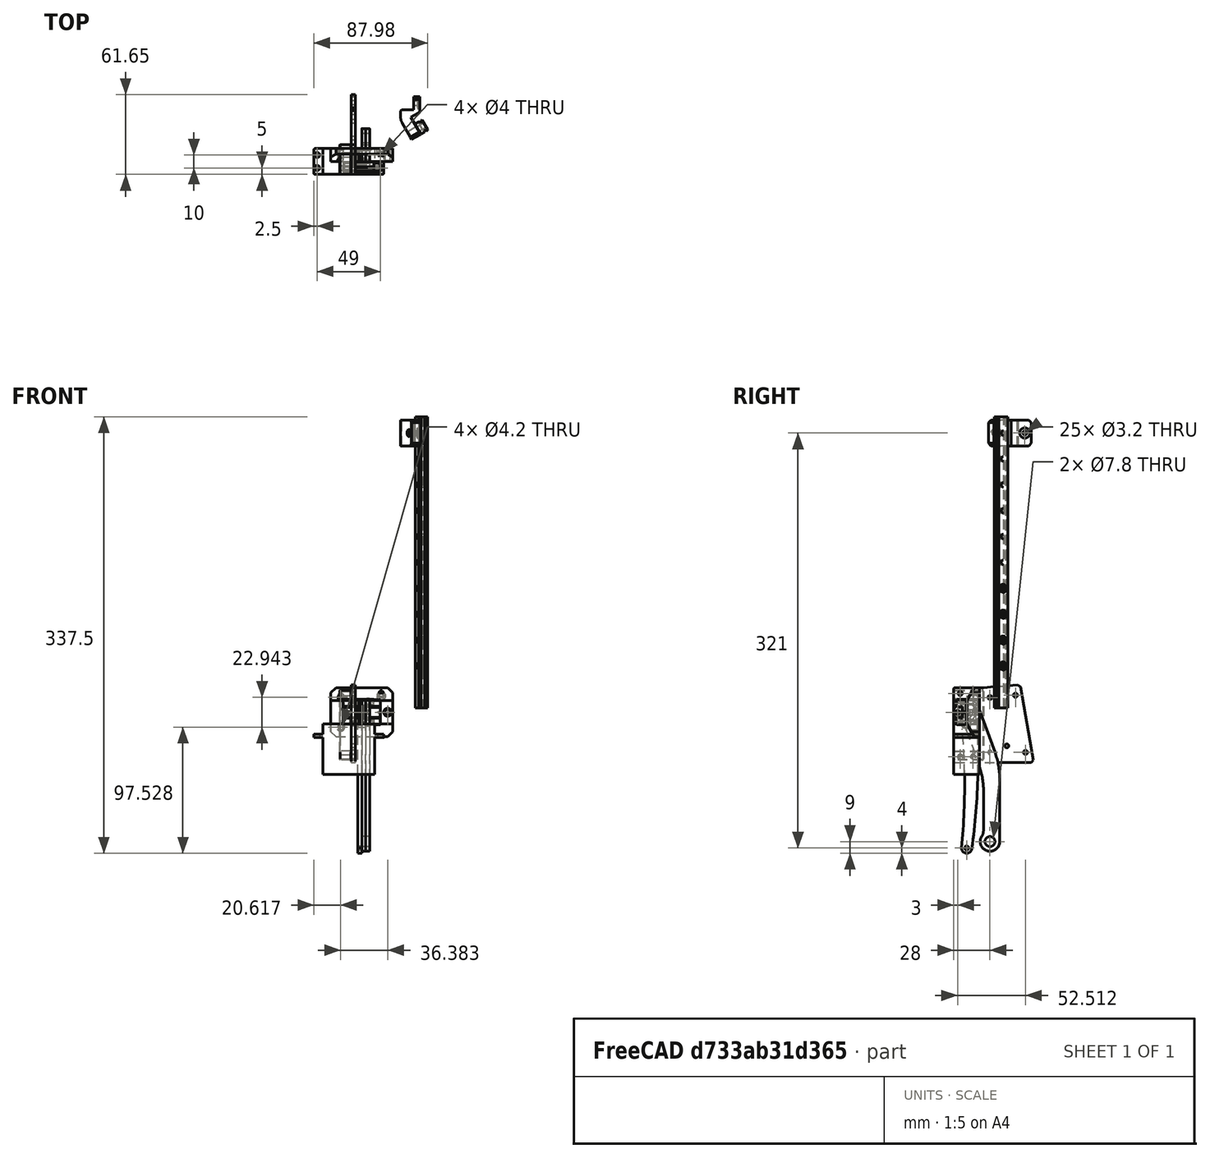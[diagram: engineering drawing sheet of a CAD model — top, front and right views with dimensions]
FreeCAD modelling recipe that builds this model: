
FCSTD DOCUMENT  (FreeCAD 1.2R20260106 (Git shallow))
Label: linear-lifter
License: All rights reserved
LicenseURL: https://en.wikipedia.org/wiki/All_rights_reserved
objects: App::FeaturePython×18, Part::Feature×15, App::Link×15, App::Point×5, App::Part×4, Assembly::JointGroup×1, Assembly::AssemblyObject×1
note: 15 computed .brp shape members not serialized (recipe doc carries the construction recipe); baked Part::Feature solids carry a one-line shape summary decoded from their .brp

FEATURE [Part::Feature] Part__Feature  label="ServoLifterPlate"
  Placement = pos=(-8,0,0) rot=(0,0,1;0rad)
  shape: bbox 3 x 61.65 x 60.3 mm, 21 faces (baked)
FEATURE [Part::Feature] Part__Feature001  label="ServoLifterSpacer"
  Placement = pos=(-8,0,0) rot=(0,0,1;0rad)
  shape: bbox 9 x 23 x 54 mm, 56 faces (baked)
FEATURE [Part::Feature] Part__Feature006  label="RoundServoHorn"
  Placement = pos=(2.274e-13,-5.72205e-06,3.05176e-05) rot=(0.171088,0.970288,0.171088;1.60095rad)
  shape: bbox 5.4 x 20 x 20 mm, 12 faces (baked)
FEATURE [Part::Feature] Part__Feature007  label="CoreMF83"
  shape: bbox 9.2 x 3 x 9.2 mm, 6 faces (baked)
FEATURE [Part::Feature] Part__Feature008  label="CoreMF001"
  shape: bbox 4.2 x 3 x 4.2 mm, 4 faces (baked)
FEATURE [App::Part] CoreMF83  label="CoreMF002"
  Group = -> [Part__Feature007,Part__Feature008]
  Origin = -> Origin002
FEATURE [App::Point] Origin003  label="Origine002"
  Role = Origin
FEATURE [Part::Feature] Part__Feature009  label="SleeveMF83"
  shape: bbox 6.8 x 2.8 x 6.8 mm, 4 faces (baked)
FEATURE [App::Part] MF83
  Group = -> [CoreMF83,Part__Feature009]
  Origin = -> Origin004
  Placement = pos=(-2.2769e-05,18,-100) rot=(0,0,1;1.5708rad)
FEATURE [App::Point] Origin005  label="Origine004"
  Role = Origin
FEATURE [Part::Feature] Part__Feature010  label="Bielle"
  Placement = pos=(3,-3.8147e-06,0) rot=(0,0,1;0rad)
  shape: bbox 3 x 35.5 x 117.5 mm, 18 faces (baked)
FEATURE [Part::Feature] Part__Feature011  label="Bielle001"
  shape: bbox 3 x 35.5 x 117.5 mm, 18 faces (baked)
FEATURE [Part::Feature] Part__Feature017  label="Body028"
  shape: bbox 3.367 x 16.32 x 116.5 mm, 9 faces (baked)
FEATURE [Part::Feature] Part__Feature018  label="ServoBody001"
  Placement = pos=(0,0,-1) rot=(0,0,1;0rad)
  shape: bbox 54 x 20 x 41 mm, 25 faces (baked)
FEATURE [Part::Feature] Part__Feature019  label="ServoAxis001"
  shape: bbox 6 x 6 x 10 mm, 4 faces (baked)
FEATURE [App::Part] MG996
  Group = -> [Part__Feature018,Part__Feature019]
  Origin = -> Origin018
  Placement = pos=(-7.6294e-06,1.90735e-06,-3.05176e-05) rot=(0.707107,0,0.707107;3.14159rad)
FEATURE [App::Point] Origin019  label="Origine018"
  Role = Origin
FEATURE [Part::Feature] Part__Feature020  label="ClipRail"
  Placement = pos=(0,-2.57492e-05,216) rot=(0,0,1;0rad)
  shape: bbox 15.57 x 32.93 x 20 mm, 24 faces (baked)
FEATURE [Part::Feature] Part__Feature023  label="MGN9-225mm-Custom"
  Placement = pos=(55.9666,32.8897,2.46922) rot=(0.447214,0.774597,-0.447214;1.82348rad)
  shape: bbox 9.729 x 10.64 x 225 mm, 62 faces (baked)
FEATURE [Part::Feature] Part__Feature024  label="mgn9c"
  Placement = pos=(8.01086e-05,-7.99998,1.62202e-06) rot=(1,0,0;0rad)
  shape: bbox 28.92 x 8.018 x 20.02 mm, 85 faces (baked)
FEATURE [Part::Feature] Part__Feature025  label="Chariot"
  shape: bbox 48 x 10 x 38 mm, 35 faces (baked)
FEATURE [App::Part] Lifter  label="linear-lifter-parts"
  Group = -> [Part__Feature,Part__Feature001,Part__Feature006,Part__Feature010,Part__Feature011,MF83,Part__Feature017,Part__Feature024,Part__Feature025,Part__Feature020,Part__Feature023,MG996]
  Origin = -> Origin028
FEATURE [App::Point] Origin029  label="Origine028"
  Role = Origin
FEATURE [App::Point] Origin030  label="Origine"
  Role = Origin
FEATURE [App::Link] MGN9_225mm_Custom  label="MGN9-225mm-Custom001"
  LinkPlacement = pos=(0,0,0) rot=(0,1,0;1.5708rad)
  LinkedObject = -> Part__Feature023
  Placement = pos=(0,0,0) rot=(0,1,0;1.5708rad)
FEATURE [App::FeaturePython] GroundedJoint  # Assembly grounded joint (typed FeaturePython)
  ObjectToGround = -> MGN9_225mm_Custom
FEATURE [App::Link] ClipRail  label="ClipRail001"
  LinkPlacement = pos=(0.499992,-64.9133,133.531) rot=(0.5,0.866025,0;3.14159rad)
  LinkedObject = -> Part__Feature020
  Placement = pos=(0.499992,-64.9133,133.531) rot=(0.5,0.866025,0;3.14159rad)
FEATURE [App::Link] ClipRail001  label="ClipRail002"
  LinkPlacement = pos=(0.499992,-64.9133,213.531) rot=(0,0,1;1.0472rad)
  LinkedObject = -> Part__Feature020
  Placement = pos=(0.499992,-64.9133,213.531) rot=(0,0,1;1.0472rad)
FEATURE [App::Link] ClipRail002  label="ClipRail003"
  LinkPlacement = pos=(0.499992,-64.9133,53.5308) rot=(0.5,0.866025,0;3.14159rad)
  LinkedObject = -> Part__Feature020
  Placement = pos=(0.499992,-64.9133,53.5308) rot=(0.5,0.866025,0;3.14159rad)
FEATURE [App::Link] Chariot  label="Chariot001"
  LinkPlacement = pos=(0.499992,-4.91335,67.3673) rot=(0,-1,0;1.5708rad)
  LinkedObject = -> Part__Feature025
  Placement = pos=(0.499992,-4.91335,67.3673) rot=(0,-1,0;1.5708rad)
FEATURE [App::Link] mgn9c  label="mgn9c001"
  LinkPlacement = pos=(0.499992,-12.9133,67.3673) rot=(0,1,0;1.5708rad)
  LinkedObject = -> Part__Feature024
  Placement = pos=(0.499992,-12.9133,67.3673) rot=(0,1,0;1.5708rad)
FEATURE [App::Link] Body028  label="Body029"
  LinkPlacement = pos=(-31.3959,8.30559,185.591) rot=(-0.157315,-0.090826,0.983363;1.06179rad)
  LinkedObject = -> Part__Feature017
  Placement = pos=(-31.3959,8.30559,185.591) rot=(-0.157315,-0.090826,0.983363;1.06179rad)
FEATURE [App::Link] MF001
  LinkPlacement = pos=(-28.0959,14.0214,185.591) rot=(0.092352,0.344662,-0.934173;0.558662rad)
  LinkedObject = -> MF83
  Placement = pos=(-28.0959,14.0214,185.591) rot=(0.092352,0.344662,-0.934173;0.558662rad)
FEATURE [App::Link] MF002
  LinkPlacement = pos=(-31.0959,8.8252,185.591) rot=(0.961552,-0.257647,-0.095058;3.19252rad)
  LinkedObject = -> MF83
  Placement = pos=(-31.0959,8.8252,185.591) rot=(0.961552,-0.257647,-0.095058;3.19252rad)
FEATURE [App::Link] Bielle001  label="Bielle002"
  LinkPlacement = pos=(2.64807,-7.19277,280.131) rot=(0.167978,0.096982,0.981009;1.06388rad)
  LinkedObject = -> Part__Feature011
  Placement = pos=(2.64807,-7.19277,280.131) rot=(0.167978,0.096982,0.981009;1.06388rad)
FEATURE [App::Link] RoundServoHorn  label="RoundServoHorn001"
  LinkPlacement = pos=(1.14807,-9.79085,280.131) rot=(0.250983,0.666109,0.702358;2.91122rad)
  LinkedObject = -> Part__Feature006
  Placement = pos=(1.14807,-9.79085,280.131) rot=(0.250983,0.666109,0.702358;2.91122rad)
FEATURE [App::Link] ServoLifterSpacer  label="ServoLifterSpacer001"
  LinkPlacement = pos=(-2.85193,-16.719,280.131) rot=(0,0,1;1.0472rad)
  LinkedObject = -> Part__Feature001
  Placement = pos=(-2.85193,-16.719,280.131) rot=(0,0,1;1.0472rad)
FEATURE [App::Link] ServoLifterPlate  label="ServoLifterPlate001"
  LinkPlacement = pos=(-2.85193,-16.719,280.131) rot=(0,0,1;1.0472rad)
  LinkedObject = -> Part__Feature
  Placement = pos=(-2.85193,-16.719,280.131) rot=(0,0,1;1.0472rad)
FEATURE [App::FeaturePython] Joint  label="Fixed"  # Assembly joint (typed FeaturePython)
  Angle = 0
  AngleMax = 0
  AngleMin = 0
  Detach1 = false
  Detach2 = false
  Distance = 0
  Distance2 = 0
  EnableAngleMax = false
  EnableAngleMin = false
  EnableLengthMax = false
  EnableLengthMin = false
  JointType = 0 (Fixed)
  LengthMax = 0
  LengthMin = 0
  Offset2 = pos=(0,0,0) rot=(0,0,-1;1.5708rad)
  Placement1 = pos=(43.3013,25,0) rot=(0.377964,0.654654,0.654654;2.41886rad)
  Placement2 = pos=(-213.531,-14.9133,0.499992) rot=(0.57735,0.57735,-0.57735;2.0944rad)
  Reference1 = -> Assembly [ClipRail001.Edge55,ClipRail001.Edge55]
  Reference2 = -> Assembly [MGN9_225mm_Custom.Edge42,MGN9_225mm_Custom.Edge42]
  Suppressed = false
FEATURE [App::FeaturePython] Joint001  label="Fixed001"  # Assembly joint (typed FeaturePython)
  Angle = 0
  AngleMax = 0
  AngleMin = 0
  Detach1 = false
  Detach2 = false
  Distance = 0
  Distance2 = 0
  EnableAngleMax = false
  EnableAngleMin = false
  EnableLengthMax = false
  EnableLengthMin = false
  JointType = 0 (Fixed)
  LengthMax = 0
  LengthMin = 0
  Offset2 = pos=(0,0,0) rot=(0,0,1;1.5708rad)
  Placement1 = pos=(43.3013,25,0) rot=(-0.377964,-0.654654,-0.654654;3.86433rad)
  Placement2 = pos=(-133.531,-14.9133,0.499992) rot=(0.57735,-0.57735,0.57735;2.0944rad)
  Reference1 = -> Assembly [ClipRail.Edge55,ClipRail.Edge55]
  Reference2 = -> Assembly [MGN9_225mm_Custom.Edge30,MGN9_225mm_Custom.Edge30]
  Suppressed = false
FEATURE [App::FeaturePython] Joint002  label="Fixed002"  # Assembly joint (typed FeaturePython)
  Angle = 0
  AngleMax = 0
  AngleMin = 0
  Detach1 = false
  Detach2 = false
  Distance = 0
  Distance2 = 0
  EnableAngleMax = false
  EnableAngleMin = false
  EnableLengthMax = false
  EnableLengthMin = false
  JointType = 0 (Fixed)
  LengthMax = 0
  LengthMin = 0
  Placement1 = pos=(43.3013,25,0) rot=(-0.377964,-0.654654,-0.654654;3.86433rad)
  Placement2 = pos=(-53.5308,-14.9133,0.499992) rot=(-0.57735,-0.57735,-0.57735;2.0944rad)
  Reference1 = -> Assembly [ClipRail002.Edge55,ClipRail002.Edge55]
  Reference2 = -> Assembly [MGN9_225mm_Custom.Edge51,MGN9_225mm_Custom.Edge51]
  Suppressed = false
FEATURE [App::FeaturePython] Joint003  label="Slider003"  # Assembly joint (typed FeaturePython)
  Angle = 0
  AngleMax = 0
  AngleMin = 0
  Detach1 = false
  Detach2 = false
  Distance = 0
  Distance2 = 0
  EnableAngleMax = false
  EnableAngleMin = false
  EnableLengthMax = false
  EnableLengthMin = false
  JointType = 3 (Slider)
  LengthMax = 0
  LengthMin = 0
  Placement1 = pos=(-14.45,2.5,-4.8) rot=(0,-1,0;1.5708rad)
  Placement2 = pos=(-1.03078,-10.4133,-4.30001) rot=(0.707107,0,0.707107;3.14159rad)
  Reference1 = -> Assembly [mgn9c.Face26,mgn9c.Edge6]
  Reference2 = -> Assembly [MGN9_225mm_Custom.Edge97,MGN9_225mm_Custom.Edge97]
  Suppressed = false
FEATURE [App::FeaturePython] Joint004  label="Fixed003"  # Assembly joint (typed FeaturePython)
  Angle = 0
  AngleMax = 0
  AngleMin = 0
  Detach1 = false
  Detach2 = false
  Distance = 0
  Distance2 = 0
  EnableAngleMax = false
  EnableAngleMin = false
  EnableLengthMax = false
  EnableLengthMin = false
  JointType = 0 (Fixed)
  LengthMax = 0
  LengthMin = 0
  Offset2 = pos=(0,0,0) rot=(0,0,1;1.5708rad)
  Placement1 = pos=(-5,3.6e-15,7.5) rot=(0,-0.707107,-0.707107;3.14159rad)
  Placement2 = pos=(5,8,-7.5) rot=(-1,0,0;1.5708rad)
  Reference1 = -> Assembly [Chariot.Edge5,Chariot.Edge5]
  Reference2 = -> Assembly [mgn9c.Edge190,mgn9c.Edge190]
  Suppressed = false
FEATURE [App::FeaturePython] Joint005  label="Revolute004"  # Assembly joint (typed FeaturePython)
  Angle = 0
  AngleMax = 0
  AngleMin = 0
  Detach1 = false
  Detach2 = false
  Distance = 0
  Distance2 = 0
  EnableAngleMax = false
  EnableAngleMin = false
  EnableLengthMax = false
  EnableLengthMin = false
  JointType = 1 (Revolute)
  LengthMax = 0
  LengthMin = 0
  Placement1 = pos=(-1.8e-15,-3.6e-15,-105) rot=(0.57735,0.57735,0.57735;2.0944rad)
  Placement2 = pos=(15,3.60289,15.2404) rot=(-1,0,0;5.23599rad)
  Reference1 = -> Assembly [Body028.Edge10,Body028.Edge10]
  Reference2 = -> Assembly [Chariot.Edge31,Chariot.Edge31]
  Suppressed = false
FEATURE [App::Link] Bielle002  label="Bielle003"
  LinkPlacement = pos=(1.14807,-9.79085,280.131) rot=(0.167978,0.096982,0.981009;1.06388rad)
  LinkedObject = -> Part__Feature011
  Placement = pos=(1.14807,-9.79085,280.131) rot=(0.167978,0.096982,0.981009;1.06388rad)
FEATURE [App::FeaturePython] Joint006  label="Fixed004"  # Assembly joint (typed FeaturePython)
  Angle = 0
  AngleMax = 0
  AngleMin = 0
  Detach1 = false
  Detach2 = false
  Distance = 0
  Distance2 = 0
  EnableAngleMax = false
  EnableAngleMin = false
  EnableLengthMax = false
  EnableLengthMin = false
  JointType = 0 (Fixed)
  LengthMax = 0
  LengthMin = 0
  Placement1 = pos=(3,18,-100) rot=(0.57735,0.57735,0.57735;2.0944rad)
  Placement2 = pos=(-2.13e-14,18,-100) rot=(0.57735,0.57735,0.57735;2.0944rad)
  Reference1 = -> Assembly [Bielle002.Edge31,Bielle002.Edge31]
  Reference2 = -> Assembly [Bielle001.Edge14,Bielle001.Edge14]
  Suppressed = false
FEATURE [App::FeaturePython] Joint008  label="Fixed006"  # Assembly joint (typed FeaturePython)
  Angle = 0
  AngleMax = 0
  AngleMin = 0
  Detach1 = false
  Detach2 = false
  Distance = 0
  Distance2 = 0
  EnableAngleMax = false
  EnableAngleMin = false
  EnableLengthMax = false
  EnableLengthMin = false
  JointType = 0 (Fixed)
  LengthMax = 0
  LengthMin = 0
  Placement1 = pos=(0,0,0) rot=(0,0.707107,0.707107;3.14159rad)
  Placement2 = pos=(3,18,-100) rot=(0.57735,0.57735,0.57735;2.0944rad)
  Reference1 = -> Assembly [MF001.CoreMF83.Part__Feature007.Edge9,MF001.CoreMF83.Part__Feature007.Edge9]
  Reference2 = -> Assembly [Bielle001.Edge31,Bielle001.Edge31]
  Suppressed = false
FEATURE [App::FeaturePython] Joint009  label="Fixed007"  # Assembly joint (typed FeaturePython)
  Angle = 0
  AngleMax = 0
  AngleMin = 0
  Detach1 = false
  Detach2 = false
  Distance = 0
  Distance2 = 0
  EnableAngleMax = false
  EnableAngleMin = false
  EnableLengthMax = false
  EnableLengthMin = false
  JointType = 0 (Fixed)
  LengthMax = 0
  LengthMin = 0
  Placement1 = pos=(0,0,0) rot=(0,0.707107,0.707107;3.14159rad)
  Placement2 = pos=(-2.22e-14,18,-100) rot=(0.57735,0.57735,0.57735;2.0944rad)
  Reference1 = -> Assembly [MF002.CoreMF83.Part__Feature007.Edge9,MF002.CoreMF83.Part__Feature007.Edge9]
  Reference2 = -> Assembly [Bielle002.Edge14,Bielle002.Edge14]
  Suppressed = false
FEATURE [App::FeaturePython] Joint010  label="Revolute009"  # Assembly joint (typed FeaturePython)
  Angle = 0
  AngleMax = 0
  AngleMin = 0
  Detach1 = false
  Detach2 = false
  Distance = 0
  Distance2 = 0
  EnableAngleMax = false
  EnableAngleMin = false
  EnableLengthMax = false
  EnableLengthMin = false
  JointType = 1 (Revolute)
  LengthMax = 0
  LengthMin = 0
  Placement1 = pos=(0,0,0) rot=(0.57735,0.57735,0.57735;2.0944rad)
  Placement2 = pos=(0,0.6,0) rot=(0,0.707107,0.707107;3.14159rad)
  Reference1 = -> Assembly [Body028.Edge9,Body028.Edge9]
  Reference2 = -> Assembly [MF002.CoreMF83.Part__Feature008.Edge2,MF002.CoreMF83.Part__Feature008.Edge2]
  Suppressed = false
FEATURE [App::FeaturePython] Joint011  label="Fixed009"  # Assembly joint (typed FeaturePython)
  Angle = 0
  AngleMax = 0
  AngleMin = 0
  Detach1 = false
  Detach2 = false
  Distance = 0
  Distance2 = 0
  EnableAngleMax = false
  EnableAngleMin = false
  EnableLengthMax = false
  EnableLengthMin = false
  JointType = 0 (Fixed)
  LengthMax = 0
  LengthMin = 0
  Placement2 = pos=(0,0,0) rot=(0.57735,0.57735,0.57735;2.0944rad)
  Reference1 = -> Assembly [RoundServoHorn.Edge24,RoundServoHorn.Edge24]
  Reference2 = -> Assembly [Bielle002.Edge19,Bielle002.Edge19]
  Suppressed = false
FEATURE [App::Link] MG997
  LinkPlacement = pos=(1.14807,-9.79085,280.131) rot=(0.654654,0.377964,0.654654;3.86433rad)
  LinkedObject = -> MG996
  Placement = pos=(1.14807,-9.79085,280.131) rot=(0.654654,0.377964,0.654654;3.86433rad)
FEATURE [App::FeaturePython] Joint012  label="Fixed010"  # Assembly joint (typed FeaturePython)
  Angle = 0
  AngleMax = 0
  AngleMin = 0
  Detach1 = false
  Detach2 = false
  Distance = 0
  Distance2 = 0
  EnableAngleMax = false
  EnableAngleMin = false
  EnableLengthMax = false
  EnableLengthMin = false
  JointType = 0 (Fixed)
  LengthMax = 0
  LengthMin = 0
  Placement1 = pos=(3.6e-15,-5,14.5) rot=(0.57735,0.57735,0.57735;2.0944rad)
  Placement2 = pos=(0,-5,14.5) rot=(0.57735,0.57735,0.57735;2.0944rad)
  Reference1 = -> Assembly [ServoLifterSpacer.Edge36,ServoLifterSpacer.Edge36]
  Reference2 = -> Assembly [ServoLifterPlate.Edge16,ServoLifterPlate.Edge16]
  Suppressed = false
FEATURE [App::FeaturePython] Joint013  label="Fixed011"  # Assembly joint (typed FeaturePython)
  Angle = 0
  AngleMax = 0
  AngleMin = 0
  Detach1 = false
  Detach2 = false
  Distance = 0
  Distance2 = 0
  EnableAngleMax = false
  EnableAngleMin = false
  EnableLengthMax = false
  EnableLengthMin = false
  JointType = 0 (Fixed)
  LengthMax = 0
  LengthMin = 0
  Offset2 = pos=(0,0,0) rot=(0,0,1;1.5708rad)
  Placement1 = pos=(14.5,5,-16) rot=(0,0,1;0rad)
  Placement2 = pos=(-9,-5,14.5) rot=(0.707107,0,0.707107;3.14159rad)
  Reference1 = -> Assembly [MG997.Part__Feature018.Edge52,MG997.Part__Feature018.Edge52]
  Reference2 = -> Assembly [ServoLifterSpacer.Edge53,ServoLifterSpacer.Edge53]
  Suppressed = false
FEATURE [App::FeaturePython] Joint014  label="Revolute012"  # Assembly joint (typed FeaturePython)
  Angle = 0
  AngleMax = 0
  AngleMin = 0
  Detach1 = false
  Detach2 = false
  Distance = 0
  Distance2 = 0
  EnableAngleMax = false
  EnableAngleMin = false
  EnableLengthMax = false
  EnableLengthMin = false
  JointType = 1 (Revolute)
  LengthMax = 0
  LengthMin = 0
  Placement1 = pos=(0,0,-2) rot=(0,0,1;0rad)
  Placement2 = pos=(0,0,-2) rot=(0,0,1;0rad)
  Reference1 = -> Assembly [MG997.Part__Feature019.Edge5,MG997.Part__Feature019.Edge5]
  Reference2 = -> Assembly [RoundServoHorn.Edge22,RoundServoHorn.Edge22]
  Suppressed = false
FEATURE [App::FeaturePython] Joint015  label="Parallel012"  # Assembly joint (typed FeaturePython)
  Angle = 0
  AngleMax = 0
  AngleMin = 0
  Detach1 = false
  Detach2 = false
  Distance = 0
  Distance2 = 0
  EnableAngleMax = false
  EnableAngleMin = false
  EnableLengthMax = false
  EnableLengthMin = false
  JointType = 6 (Parallel)
  LengthMax = 0
  LengthMin = 0
  Placement1 = pos=(1.5,-10,-10) rot=(0.57735,-0.57735,-0.57735;4.18879rad)
  Placement2 = pos=(42.5,50,0) rot=(-1,0,0;1.5708rad)
  Reference1 = -> Assembly [ServoLifterPlate.Face6,ServoLifterPlate.Face6]
  Reference2 = -> Assembly [ClipRail001.Face21,ClipRail001.Face21]
  Suppressed = false
FEATURE [App::FeaturePython] Joint016  label="Distance013"  # Assembly joint (typed FeaturePython)
  Angle = 0
  AngleMax = 0
  AngleMin = 0
  Detach1 = false
  Detach2 = false
  Distance = -17.6
  Distance2 = 0
  EnableAngleMax = false
  EnableAngleMin = false
  EnableLengthMax = false
  EnableLengthMin = false
  JointType = 5 (Distance)
  LengthMax = 0
  LengthMin = 0
  Placement1 = pos=(1.5,20.5,-39) rot=(0,0,1;1.5708rad)
  Placement2 = pos=(37.8607,33.2868,10) rot=(0,0,1;0rad)
  Reference1 = -> Assembly [ServoLifterPlate.Face2,ServoLifterPlate.Face2]
  Reference2 = -> Assembly [ClipRail001.Face6,ClipRail001.Edge9]
  Suppressed = false
FEATURE [App::FeaturePython] Joint017  label="Distance014"  # Assembly joint (typed FeaturePython)
  Angle = 0
  AngleMax = 0
  AngleMin = 0
  Detach1 = false
  Detach2 = false
  Distance = -33
  Distance2 = 0
  EnableAngleMax = false
  EnableAngleMin = false
  EnableLengthMax = false
  EnableLengthMin = false
  JointType = 5 (Distance)
  LengthMax = 0
  LengthMin = 0
  Placement1 = pos=(42.5,50,0) rot=(-1,0,0;1.5708rad)
  Placement2 = pos=(1.5,-10,-10) rot=(0.57735,-0.57735,-0.57735;4.18879rad)
  Reference1 = -> Assembly [ClipRail001.Face21,ClipRail001.Face21]
  Reference2 = -> Assembly [ServoLifterPlate.Face6,ServoLifterPlate.Face6]
  Suppressed = false
FEATURE [Assembly::JointGroup] Joints
  Group = -> [GroundedJoint,Joint,Joint001,Joint002,Joint003,Joint004,Joint005,Joint006,Joint008,Joint009,Joint010,Joint011,Joint012,Joint013,Joint014,Joint015,Joint016,Joint017]
FEATURE [Assembly::AssemblyObject] Assembly  label="linear-lifter-asm"
  Group = -> [Joints,MGN9_225mm_Custom,GroundedJoint,ClipRail,ClipRail001,ClipRail002,Chariot,mgn9c,Body028,MF001,MF002,Bielle001,RoundServoHorn,ServoLifterSpacer,ServoLifterPlate,Joint,Joint001,Joint002,Joint003,Joint004,Joint005,Bielle002,Joint006,Joint008,Joint009,Joint010,Joint011,MG997,Joint012,Joint013,Joint014,Joint015,Joint016,Joint017]
  Origin = -> Origin
  Type = Assembly
